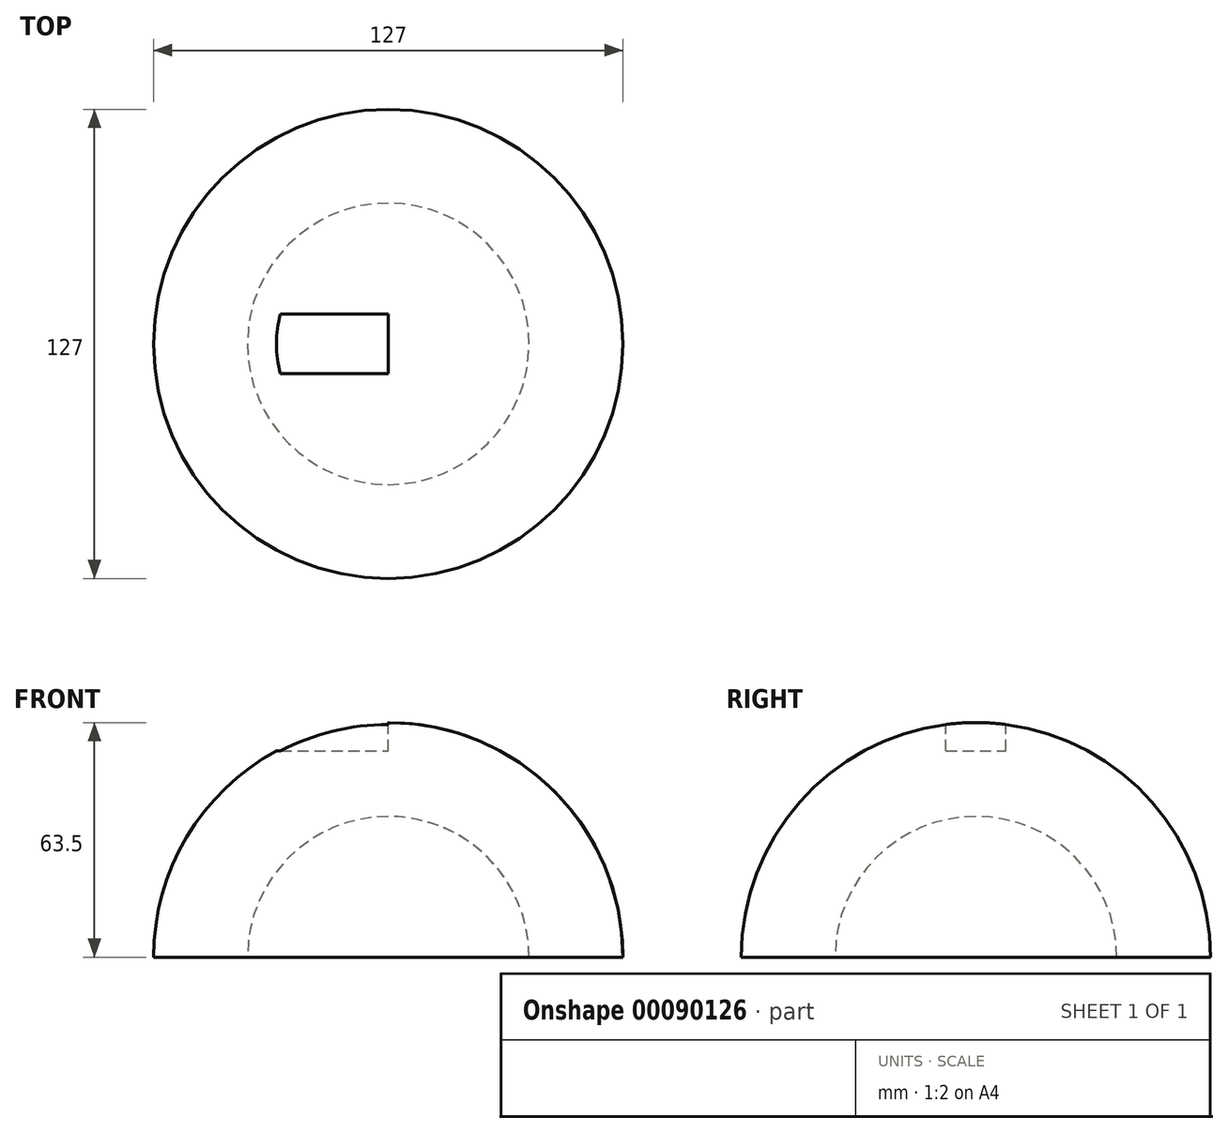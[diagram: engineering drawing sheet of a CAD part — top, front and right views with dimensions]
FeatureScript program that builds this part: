
annotation { "Feature Type Name" : "Feature", "Feature Type Description" : "" }
export const myFeature = defineFeature(function(context is Context, id is Id, definition is map)
    precondition{}
    {
        {
            var Q0;
            Q0=qCreatedBy(makeId("Front.planeOp"),FACE);
            var sketch = newSketch(context, id + "F0", { "sketchPlane" : qUnion([Q0])});
            skArc(sketch, "E0", {"start": v(63.5, 0) * mm, "mid": v(44.9, 44.9) * mm, "end": v(0, 63.5) * mm});
            skArc(sketch, "E1", {"start": v(38.1, 0) * mm, "mid": v(26.94, 26.94) * mm, "end": v(0, 38.1) * mm});
            skLineSegment(sketch, "E2", {"start": v(0, 63.5) * mm, "end": v(0, 38.1) * mm});
            skLineSegment(sketch, "E3", {"start": v(38.1, 0) * mm, "end": v(63.5, 0) * mm});
            skLineSegment(sketch, "E4", {"start": v(0, 105.14) * mm, "end": v(0, -105.65) * mm, "construction": true});
            skSolve(sketch);
        }
        {
            var Q0;
            Q0 = qSketchRegion(id + "F0", true);
            var Q1;
            Q1=sQuery(id+"F0.wireOp",EDGE,"E4");
            revolve(context, id + "F1", {"entities" : qUnion([Q0]), "axis" : qUnion([Q1]), "revolveType" : RevolveType.FULL});
        }
        {
            var Q0;
            Q0=qCreatedBy(makeId("Right.planeOp"),FACE);
            var sketch = newSketch(context, id + "F2", { "sketchPlane" : qUnion([Q0])});
            skLineSegment(sketch, "E5.bottom", {"start": v(-8.1, 55.82) * mm, "end": v(8.1, 55.82) * mm});
            skLineSegment(sketch, "E5.top", {"start": v(-8.1, 73.56) * mm, "end": v(8.1, 73.56) * mm});
            skLineSegment(sketch, "E5.left", {"start": v(-8.1, 55.82) * mm, "end": v(-8.1, 73.56) * mm});
            skLineSegment(sketch, "E5.right", {"start": v(8.1, 55.82) * mm, "end": v(8.1, 73.56) * mm});
            skPoint(sketch, "E5.middle", {"position": v(0, 64.7) * mm});
            skSolve(sketch);
        }
        {
            var Q0;
            Q0=makeQuery(id+"F2.imprint","IMPRINT",FACE,{"disambiguationData":[TD([[makeQuery(id+"F2.imprint","IMPRINT",EDGE,{"derivedFrom":sQuery(id+"F2.wireOp",EDGE,"E5.bottom")}),1.0]])]});
            extrude(context, id + "F3", {"entities" : qUnion([Q0]), "operationType" : NewBodyOperationType.REMOVE, "endBound" : BoundingType.THROUGH_ALL, "oppositeDirection" : true, "depth" : 25.4 * mm});
        }
    });
